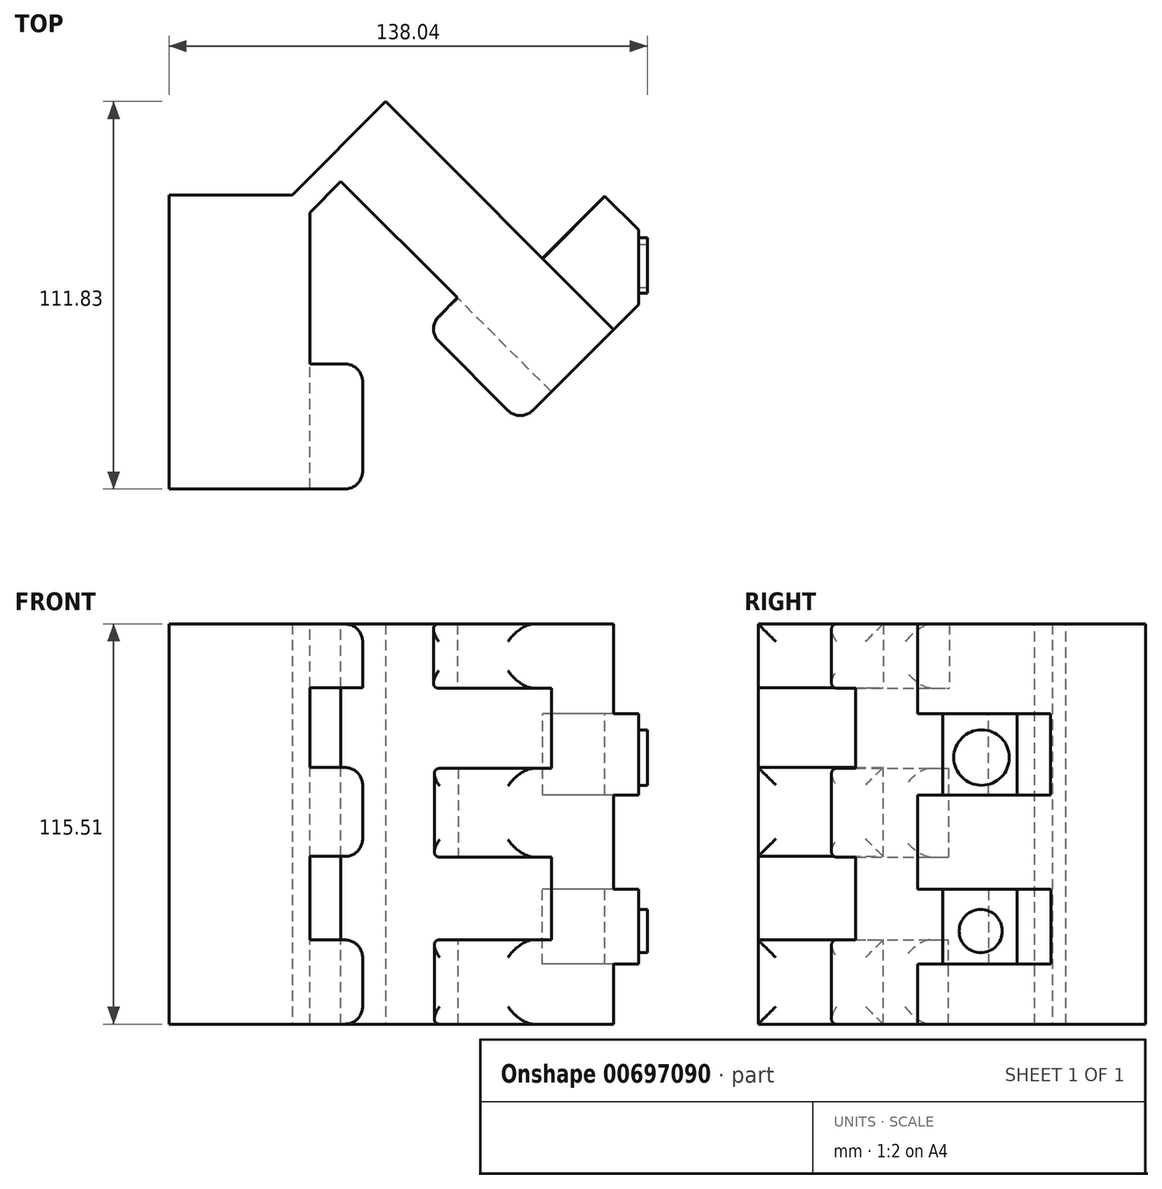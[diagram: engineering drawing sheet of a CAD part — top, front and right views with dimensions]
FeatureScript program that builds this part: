
annotation { "Feature Type Name" : "Feature", "Feature Type Description" : "" }
export const myFeature = defineFeature(function(context is Context, id is Id, definition is map)
    precondition{}
    {
        {
            var Q0;
            Q0=qCreatedBy(makeId("Right.planeOp"),FACE);
            var sketch = newSketch(context, id + "F0", { "sketchPlane" : qUnion([Q0])});
            skLineSegment(sketch, "E0.bottom", {"start": v(-36.06, -39) * mm, "end": v(48.83, -39) * mm});
            skLineSegment(sketch, "E0.top", {"start": v(-36.06, 38.4) * mm, "end": v(48.83, 38.4) * mm});
            skLineSegment(sketch, "E0.left", {"start": v(-36.06, -39) * mm, "end": v(-36.06, 38.4) * mm});
            skLineSegment(sketch, "E0.right", {"start": v(48.83, -39) * mm, "end": v(48.83, 38.4) * mm});
            skSolve(sketch);
        }
        {
            var Q0;
            Q0=makeQuery(id+"F0.imprint","IMPRINT",FACE,{"disambiguationData":[TD([[makeQuery(id+"F0.imprint","IMPRINT",EDGE,{"derivedFrom":sQuery(id+"F0.wireOp",EDGE,"E0.bottom")}),1.0]])]});
            extrude(context, id + "F1", {"entities" : qUnion([Q0]), "oppositeDirection" : true, "depth" : 40.64 * mm, "offsetDistance" : 25.4 * mm});
        }
        {
            var Q0;
            Q0=makeQuery(id+"F1.opExtrude","SWEPT_FACE",FACE,{"disambiguationData":[OSD([sQuery(id+"F0.wireOp",EDGE,"E0.top")])]});
            extrude(context, id + "F2", {"entities" : qUnion([Q0]), "operationType" : NewBodyOperationType.ADD, "depth" : 38.1 * mm, "offsetDistance" : 25.4 * mm});
        }
        {
            var Q0;
            {var subQ0=sQuery(id+"F0.wireOp",EDGE,"E0.right");var subQ1=sQuery(id+"F0.wireOp",EDGE,"E0.top");Q0=makeQuery(id+"F2.boolean.opBoolean","MERGE",EDGE,{"derivedFrom":[makeQuery(id+"F1.opExtrude","CAP_EDGE",EDGE,{"disambiguationData":[OSD([subQ0])],"isStart":true}),makeQuery(id+"F2.opExtrude","SWEPT_EDGE",EDGE,{"disambiguationData":[OSD([subQ1,subQ0]),TDD([makeQuery(id+"F1.opExtrude","CAP_VERTEX",VERTEX,{"disambiguationData":[OSD([subQ1,subQ0])],"isStart":true})])]})]});}
            chamfer(context, id + "F3", {"entities" : qUnion([Q0]), "width" : 5.08 * mm, "tangentPropagation" : true});
        }
        {
            var Q0;
            Q0=makeQuery(id+"F3.opChamfer","BLEND_FACE",FACE,{"disambiguationData":[OSD([sQuery(id+"F0.wireOp",EDGE,"E0.top"),sQuery(id+"F0.wireOp",EDGE,"E0.right")])]});
            extrude(context, id + "F4", {"entities" : qUnion([Q0]), "operationType" : NewBodyOperationType.ADD, "depth" : 12.7 * mm, "offsetDistance" : 25.4 * mm});
        }
        {
            var Q0;
            Q0=makeQuery(id+"F4.opExtrude","CAP_FACE",FACE,{"disambiguationData":[OSD([sQuery(id+"F0.wireOp",EDGE,"E0.top"),sQuery(id+"F0.wireOp",EDGE,"E0.right")])],"isStart":false});
            var sketch = newSketch(context, id + "F5", { "sketchPlane" : qUnion([Q0])});
            skLineSegment(sketch, "E1.bottom", {"start": v(38.12, 76.5) * mm, "end": v(-54.95, 76.5) * mm});
            skLineSegment(sketch, "E1.top", {"start": v(38.12, -39) * mm, "end": v(-54.95, -39) * mm});
            skLineSegment(sketch, "E1.left", {"start": v(38.12, 76.5) * mm, "end": v(38.12, -39) * mm});
            skLineSegment(sketch, "E1.right", {"start": v(-54.95, 76.5) * mm, "end": v(-54.95, -39) * mm});
            skSolve(sketch);
        }
        {
            var Q0;
            Q0 = qSketchRegion(id + "F5", true);
            extrude(context, id + "F6", {"entities" : qUnion([Q0]), "operationType" : NewBodyOperationType.ADD, "depth" : 25.4 * mm, "offsetDistance" : 25.4 * mm});
        }
        {
            var Q0;
            {var subQ0=sQuery(id+"F0.wireOp",EDGE,"E0.top");Q0=makeQuery(id+"F2.boolean.opBoolean","MERGE",FACE,{"derivedFrom":[makeQuery(id+"F1.opExtrude","CAP_FACE",FACE,{"disambiguationData":[OSD([sQuery(id+"F0.wireOp",EDGE,"E0.bottom"),subQ0,sQuery(id+"F0.wireOp",EDGE,"E0.left"),sQuery(id+"F0.wireOp",EDGE,"E0.right")])],"isStart":true}),makeQuery(id+"F2.opExtrude","SWEPT_FACE",FACE,{"disambiguationData":[OSD([subQ0]),TDD([makeQuery(id+"F1.opExtrude","CAP_EDGE",EDGE,{"disambiguationData":[OSD([subQ0])],"isStart":true})])]})]});}
            var sketch = newSketch(context, id + "F7", { "sketchPlane" : qUnion([Q0])});
            skLineSegment(sketch, "E2.bottom", {"start": v(-36.06, -39) * mm, "end": v(0, -39) * mm});
            skLineSegment(sketch, "E2.top", {"start": v(-36.06, -14.7) * mm, "end": v(0, -14.7) * mm});
            skLineSegment(sketch, "E2.left", {"start": v(-36.06, -39) * mm, "end": v(-36.06, -14.7) * mm});
            skLineSegment(sketch, "E2.right", {"start": v(0, -39) * mm, "end": v(0, -14.7) * mm});
            skLineSegment(sketch, "E3.top", {"start": v(-36.06, 58.15) * mm, "end": v(0, 58.15) * mm});
            skLineSegment(sketch, "E4.bottom", {"start": v(-36.06, 76.5) * mm, "end": v(0, 76.5) * mm});
            skLineSegment(sketch, "E4.left", {"start": v(-36.06, 76.5) * mm, "end": v(-36.06, 58.15) * mm});
            skLineSegment(sketch, "E4.right", {"start": v(0, 76.5) * mm, "end": v(0, 58.15) * mm});
            skLineSegment(sketch, "E5.bottom", {"start": v(-36.06, 9.42) * mm, "end": v(0, 9.42) * mm});
            skLineSegment(sketch, "E5.top", {"start": v(-36.06, 35.1) * mm, "end": v(0, 35.1) * mm});
            skLineSegment(sketch, "E5.left", {"start": v(-36.06, 9.42) * mm, "end": v(-36.06, 35.1) * mm});
            skLineSegment(sketch, "E5.right", {"start": v(0, 9.42) * mm, "end": v(0, 35.1) * mm});
            skSolve(sketch);
        }
        {
            var Q0;
            Q0=makeQuery(id+"F7.imprint","IMPRINT",FACE,{"disambiguationData":[TD([[makeQuery(id+"F7.imprint","IMPRINT",EDGE,{"derivedFrom":sQuery(id+"F7.wireOp",EDGE,"E5.bottom")}),1.0]])]});
            var Q1;
            Q1=makeQuery(id+"F7.imprint","IMPRINT",FACE,{"disambiguationData":[TD([[makeQuery(id+"F7.imprint","IMPRINT",EDGE,{"derivedFrom":sQuery(id+"F7.wireOp",EDGE,"E4.bottom")}),-1.0]])]});
            var Q2;
            Q2=makeQuery(id+"F7.imprint","IMPRINT",FACE,{"disambiguationData":[TD([[makeQuery(id+"F7.imprint","IMPRINT",EDGE,{"derivedFrom":sQuery(id+"F7.wireOp",EDGE,"E2.bottom")}),1.0]])]});
            extrude(context, id + "F8", {"entities" : qUnion([Q0, Q1, Q2]), "operationType" : NewBodyOperationType.ADD, "depth" : 15.24 * mm, "offsetDistance" : 25.4 * mm});
        }
        {
            var Q0;
            Q0=makeQuery(id+"F6.opExtrude","CAP_FACE",FACE,{"disambiguationData":[OSD([sQuery(id+"F5.wireOp",EDGE,"E1.bottom"),sQuery(id+"F5.wireOp",EDGE,"E1.top"),sQuery(id+"F5.wireOp",EDGE,"E1.left"),sQuery(id+"F5.wireOp",EDGE,"E1.right")])],"isStart":true});
            var sketch = newSketch(context, id + "F9", { "sketchPlane" : qUnion([Q0])});
            skLineSegment(sketch, "E6.bottom", {"start": v(54.95, 76.5) * mm, "end": v(16.57, 76.5) * mm});
            skLineSegment(sketch, "E6.top", {"start": v(54.95, 58) * mm, "end": v(16.57, 58) * mm});
            skLineSegment(sketch, "E6.left", {"start": v(54.95, 76.5) * mm, "end": v(54.95, 58) * mm});
            skLineSegment(sketch, "E6.right", {"start": v(16.57, 76.5) * mm, "end": v(16.57, 58) * mm});
            skLineSegment(sketch, "E7.bottom", {"start": v(54.95, 34.82) * mm, "end": v(16.94, 34.82) * mm});
            skLineSegment(sketch, "E7.top", {"start": v(54.95, 9.24) * mm, "end": v(16.94, 9.24) * mm});
            skLineSegment(sketch, "E7.left", {"start": v(54.95, 34.82) * mm, "end": v(54.95, 9.24) * mm});
            skLineSegment(sketch, "E7.right", {"start": v(16.94, 34.82) * mm, "end": v(16.94, 9.24) * mm});
            skLineSegment(sketch, "E8.bottom", {"start": v(54.95, -39) * mm, "end": v(16.94, -39) * mm});
            skLineSegment(sketch, "E8.top", {"start": v(54.95, -14.67) * mm, "end": v(16.94, -14.67) * mm});
            skLineSegment(sketch, "E8.left", {"start": v(54.95, -39) * mm, "end": v(54.95, -14.67) * mm});
            skLineSegment(sketch, "E8.right", {"start": v(16.94, -39) * mm, "end": v(16.94, -14.67) * mm});
            skSolve(sketch);
        }
        {
            var Q0;
            Q0=makeQuery(id+"F9.imprint","IMPRINT",FACE,{"disambiguationData":[TD([[makeQuery(id+"F9.imprint","IMPRINT",EDGE,{"derivedFrom":sQuery(id+"F9.wireOp",EDGE,"E8.bottom")}),1.0]])]});
            var Q1;
            Q1=makeQuery(id+"F9.imprint","IMPRINT",FACE,{"disambiguationData":[TD([[makeQuery(id+"F9.imprint","IMPRINT",EDGE,{"derivedFrom":sQuery(id+"F9.wireOp",EDGE,"E7.bottom")}),1.0]])]});
            var Q2;
            Q2=makeQuery(id+"F9.imprint","IMPRINT",FACE,{"disambiguationData":[TD([[makeQuery(id+"F9.imprint","IMPRINT",EDGE,{"derivedFrom":sQuery(id+"F9.wireOp",EDGE,"E6.bottom")}),-1.0]])]});
            extrude(context, id + "F10", {"entities" : qUnion([Q0, Q1, Q2]), "operationType" : NewBodyOperationType.ADD, "depth" : 12.7 * mm, "offsetDistance" : 25.4 * mm});
        }
        {
            var Q0;
            Q0=makeQuery(id+"F8.opExtrude","CAP_EDGE",EDGE,{"disambiguationData":[OSD([sQuery(id+"F7.wireOp",EDGE,"E4.left")])],"isStart":false});
            var Q1;
            Q1=makeQuery(id+"F8.opExtrude","CAP_EDGE",EDGE,{"disambiguationData":[OSD([sQuery(id+"F7.wireOp",EDGE,"E4.bottom")])],"isStart":false});
            var Q2;
            Q2=makeQuery(id+"F8.opExtrude","CAP_EDGE",EDGE,{"disambiguationData":[OSD([sQuery(id+"F7.wireOp",EDGE,"E4.right")])],"isStart":false});
            var Q3;
            Q3=makeQuery(id+"F8.opExtrude","CAP_EDGE",EDGE,{"disambiguationData":[OSD([sQuery(id+"F7.wireOp",EDGE,"E5.top")])],"isStart":false});
            var Q4;
            Q4=makeQuery(id+"F8.opExtrude","CAP_EDGE",EDGE,{"disambiguationData":[OSD([sQuery(id+"F7.wireOp",EDGE,"E5.left")])],"isStart":false});
            var Q5;
            Q5=makeQuery(id+"F8.opExtrude","CAP_FACE",FACE,{"disambiguationData":[OSD([sQuery(id+"F7.wireOp",EDGE,"E5.bottom"),sQuery(id+"F7.wireOp",EDGE,"E5.top"),sQuery(id+"F7.wireOp",EDGE,"E5.left"),sQuery(id+"F7.wireOp",EDGE,"E5.right")])],"isStart":false});
            var Q6;
            Q6=makeQuery(id+"F8.opExtrude","CAP_FACE",FACE,{"disambiguationData":[OSD([sQuery(id+"F7.wireOp",EDGE,"E2.bottom"),sQuery(id+"F7.wireOp",EDGE,"E2.top"),sQuery(id+"F7.wireOp",EDGE,"E2.left"),sQuery(id+"F7.wireOp",EDGE,"E2.right")])],"isStart":false});
            var Q7;
            Q7=makeQuery(id+"F10.opExtrude","CAP_FACE",FACE,{"disambiguationData":[OSD([sQuery(id+"F9.wireOp",EDGE,"E6.bottom"),sQuery(id+"F9.wireOp",EDGE,"E6.top"),sQuery(id+"F9.wireOp",EDGE,"E6.left"),sQuery(id+"F9.wireOp",EDGE,"E6.right")])],"isStart":false});
            var Q8;
            Q8=makeQuery(id+"F10.opExtrude","CAP_FACE",FACE,{"disambiguationData":[OSD([sQuery(id+"F9.wireOp",EDGE,"E7.bottom"),sQuery(id+"F9.wireOp",EDGE,"E7.top"),sQuery(id+"F9.wireOp",EDGE,"E7.left"),sQuery(id+"F9.wireOp",EDGE,"E7.right")])],"isStart":false});
            var Q9;
            Q9=makeQuery(id+"F10.opExtrude","CAP_FACE",FACE,{"disambiguationData":[OSD([sQuery(id+"F9.wireOp",EDGE,"E8.bottom"),sQuery(id+"F9.wireOp",EDGE,"E8.top"),sQuery(id+"F9.wireOp",EDGE,"E8.left"),sQuery(id+"F9.wireOp",EDGE,"E8.right")])],"isStart":false});
            fillet(context, id + "F11", {"entities" : qUnion([Q0, Q1, Q2, Q3, Q4, Q5, Q6, Q7, Q8, Q9]), "radius" : 5.08 * mm, "tangentPropagation" : true, "allowEdgeOverflow" : false});
        }
        {
            var Q0;
            Q0=makeQuery(id+"F6.opExtrude","CAP_FACE",FACE,{"disambiguationData":[OSD([sQuery(id+"F5.wireOp",EDGE,"E1.bottom"),sQuery(id+"F5.wireOp",EDGE,"E1.top"),sQuery(id+"F5.wireOp",EDGE,"E1.left"),sQuery(id+"F5.wireOp",EDGE,"E1.right")])],"isStart":false});
            var sketch = newSketch(context, id + "F12", { "sketchPlane" : qUnion([Q0])});
            skLineSegment(sketch, "E9.bottom", {"start": v(-54.95, -21.69) * mm, "end": v(-25.87, -21.69) * mm});
            skLineSegment(sketch, "E9.top", {"start": v(-54.95, 0) * mm, "end": v(-25.87, 0) * mm});
            skLineSegment(sketch, "E9.left", {"start": v(-54.95, -21.69) * mm, "end": v(-54.95, 0) * mm});
            skLineSegment(sketch, "E9.right", {"start": v(-25.87, -21.69) * mm, "end": v(-25.87, 0) * mm});
            skLineSegment(sketch, "E10.bottom", {"start": v(-54.95, 27.16) * mm, "end": v(-26.02, 27.16) * mm});
            skLineSegment(sketch, "E10.top", {"start": v(-54.95, 50.6) * mm, "end": v(-26.02, 50.6) * mm});
            skLineSegment(sketch, "E10.left", {"start": v(-54.95, 27.16) * mm, "end": v(-54.95, 50.6) * mm});
            skLineSegment(sketch, "E10.right", {"start": v(-26.02, 27.16) * mm, "end": v(-26.02, 50.6) * mm});
            skSolve(sketch);
        }
        {
            var Q0;
            Q0 = qSketchRegion(id + "F12", true);
            extrude(context, id + "F13", {"entities" : qUnion([Q0]), "operationType" : NewBodyOperationType.ADD, "depth" : 25.4 * mm, "offsetDistance" : 25.4 * mm});
        }
        {
            var Q0;
            Q0=makeQuery(id+"F13.opExtrude","CAP_EDGE",EDGE,{"disambiguationData":[OSD([sQuery(id+"F12.wireOp",EDGE,"E10.left")])],"isStart":false});
            var Q1;
            Q1=makeQuery(id+"F13.opExtrude","CAP_EDGE",EDGE,{"disambiguationData":[OSD([sQuery(id+"F12.wireOp",EDGE,"E9.left")])],"isStart":false});
            chamfer(context, id + "F14", {"entities" : qUnion([Q0, Q1]), "width" : 15.24 * mm, "tangentPropagation" : true});
        }
        {
            var Q0;
            Q0=makeQuery(id+"F14.opChamfer","BLEND_FACE",FACE,{"disambiguationData":[OSD([sQuery(id+"F12.wireOp",EDGE,"E10.left")])]});
            var sketch = newSketch(context, id + "F15", { "sketchPlane" : qUnion([Q0])});
            skCircle(sketch, "E11", {"center": v(28.4, 37.95) * mm, "radius": 8 * mm});
            skCircle(sketch, "E12", {"center": v(28.16, -12.15) * mm, "radius": 6.23 * mm});
            skSolve(sketch);
        }
        {
            var Q0;
            Q0 = qSketchRegion(id + "F15", true);
            extrude(context, id + "F16", {"entities" : qUnion([Q0]), "operationType" : NewBodyOperationType.ADD, "depth" : 2.54 * mm, "offsetDistance" : 25.4 * mm});
        }
    });
